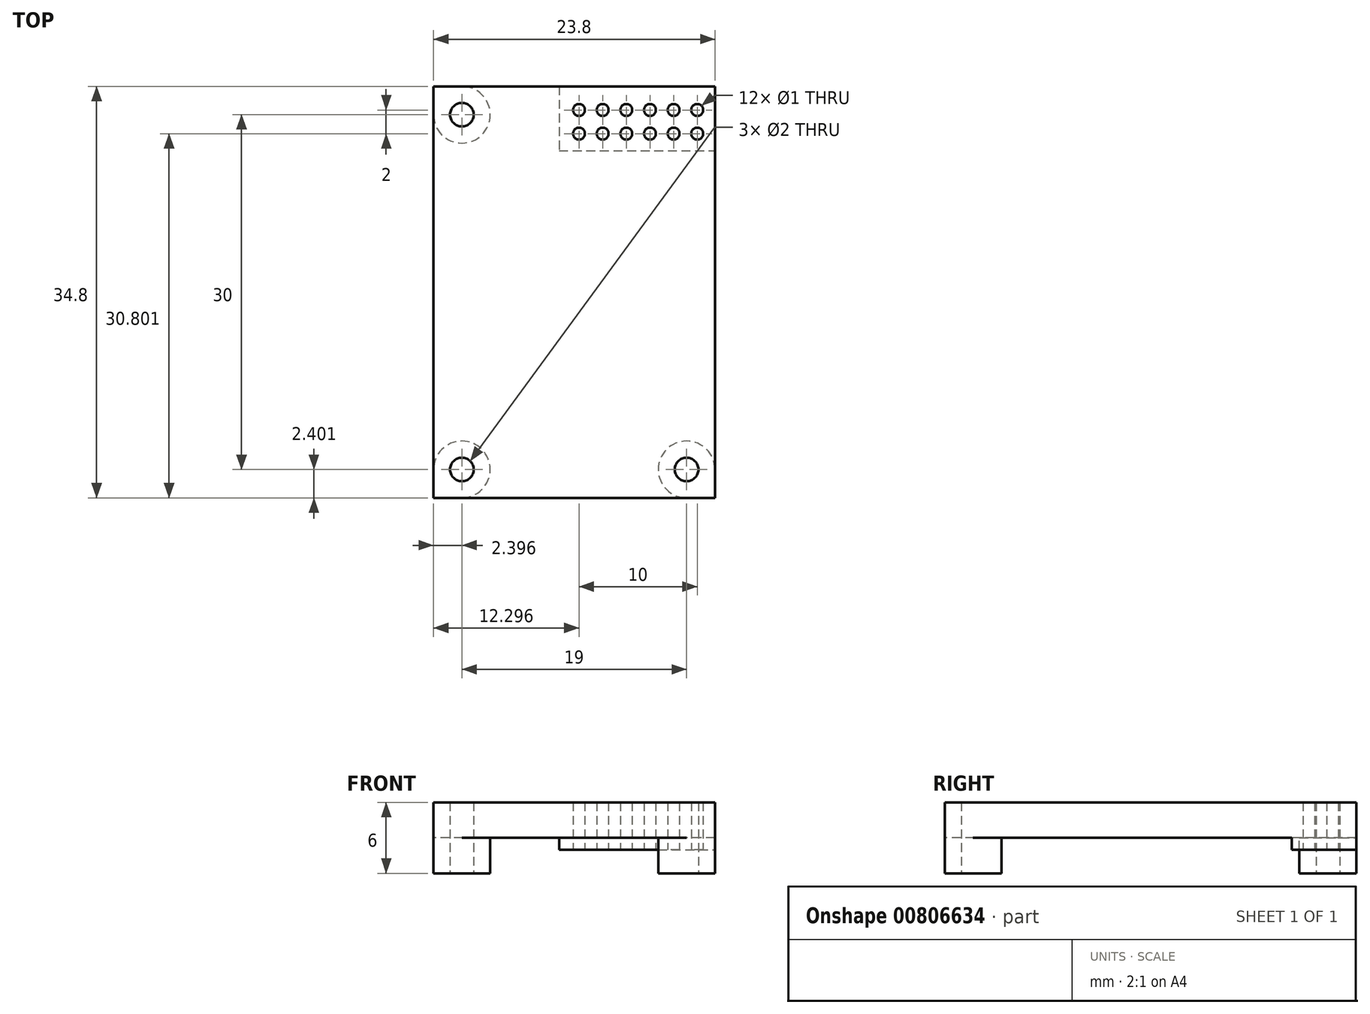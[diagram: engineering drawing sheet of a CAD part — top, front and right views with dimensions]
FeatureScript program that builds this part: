
annotation { "Feature Type Name" : "Feature", "Feature Type Description" : "" }
export const myFeature = defineFeature(function(context is Context, id is Id, definition is map)
    precondition{}
    {
        {
            var Q0;
            Q0=qCreatedBy(makeId("Top.planeOp"),FACE);
            var sketch = newSketch(context, id + "F0", { "sketchPlane" : qUnion([Q0])});
            skLineSegment(sketch, "E0.bottom", {"start": v(-2.78, 3.21) * mm, "end": v(21.02, 3.21) * mm});
            skLineSegment(sketch, "E0.top", {"start": v(-2.78, -31.59) * mm, "end": v(21.02, -31.59) * mm});
            skLineSegment(sketch, "E0.left", {"start": v(-2.78, 3.21) * mm, "end": v(-2.78, -31.59) * mm});
            skLineSegment(sketch, "E0.right", {"start": v(21.02, 3.21) * mm, "end": v(21.02, -31.59) * mm});
            skLineSegment(sketch, "E1", {"start": v(8.52, 3.21) * mm, "end": v(8.52, -1.29) * mm, "construction": true});
            skLineSegment(sketch, "E2", {"start": v(8.52, -1.29) * mm, "end": v(21.02, -1.29) * mm, "construction": true});
            skCircle(sketch, "E3", {"center": v(9.52, -0.79) * mm, "radius": 0.5 * mm});
            skCircle(sketch, "E4.1.0.0", {"center": v(11.52, -0.79) * mm, "radius": 0.5 * mm});
            skCircle(sketch, "E4.2.0.0", {"center": v(13.52, -0.79) * mm, "radius": 0.5 * mm});
            skCircle(sketch, "E4.3.0.0", {"center": v(15.52, -0.79) * mm, "radius": 0.5 * mm});
            skCircle(sketch, "E4.4.0.0", {"center": v(17.52, -0.79) * mm, "radius": 0.5 * mm});
            skCircle(sketch, "E4.5.0.0", {"center": v(19.52, -0.79) * mm, "radius": 0.5 * mm});
            skLineSegment(sketch, "E4.direction1", {"start": v(9.52, -0.79) * mm, "end": v(11.52, -0.79) * mm, "construction": true});
            skLineSegment(sketch, "E5", {"start": v(8.93, 0.21) * mm, "end": v(19.83, 0.21) * mm, "construction": true});
            skCircle(sketch, "E6.MirrorC", {"center": v(9.52, 1.21) * mm, "radius": 0.5 * mm});
            skCircle(sketch, "E7.MirrorC", {"center": v(11.52, 1.21) * mm, "radius": 0.5 * mm});
            skCircle(sketch, "E8.MirrorC", {"center": v(13.52, 1.21) * mm, "radius": 0.5 * mm});
            skCircle(sketch, "E9.MirrorC", {"center": v(15.52, 1.21) * mm, "radius": 0.5 * mm});
            skCircle(sketch, "E10.MirrorC", {"center": v(17.52, 1.21) * mm, "radius": 0.5 * mm});
            skCircle(sketch, "E11.MirrorC", {"center": v(19.52, 1.21) * mm, "radius": 0.5 * mm});
            skLineSegment(sketch, "E12", {"start": v(-2.78, -14.19) * mm, "end": v(21.02, -14.19) * mm, "construction": true});
            skLineSegment(sketch, "E13", {"start": v(9.12, -31.59) * mm, "end": v(9.12, 3.21) * mm, "construction": true});
            skLineSegment(sketch, "E14.bottom", {"start": v(-0.38, 0.81) * mm, "end": v(18.62, 0.81) * mm, "construction": true});
            skLineSegment(sketch, "E14.top", {"start": v(-0.38, -29.19) * mm, "end": v(18.62, -29.19) * mm, "construction": true});
            skLineSegment(sketch, "E14.left", {"start": v(-0.38, 0.81) * mm, "end": v(-0.38, -29.19) * mm, "construction": true});
            skLineSegment(sketch, "E14.right", {"start": v(18.62, 0.81) * mm, "end": v(18.62, -29.19) * mm, "construction": true});
            skPoint(sketch, "E14.middle", {"position": v(9.12, -14.19) * mm});
            skCircle(sketch, "E15", {"center": v(-0.38, 0.81) * mm, "radius": 1 * mm});
            skCircle(sketch, "E16", {"center": v(-0.38, -29.19) * mm, "radius": 1 * mm});
            skCircle(sketch, "E17", {"center": v(18.62, -29.19) * mm, "radius": 1 * mm});
            skSolve(sketch);
        }
        {
            var Q0;
            Q0=qSketchRegion(id+"F0",true);
            extrude(context, id + "F1", {"entities" : qUnion([Q0]), "depth" : 3 * mm, "offsetDistance" : 25 * mm});
        }
        {
            var Q0;
            Q0=makeQuery(id+"F1.opExtrude","CAP_FACE",FACE,{"disambiguationData":[OSD([sQuery(id+"F0.wireOp",EDGE,"E0.bottom"),sQuery(id+"F0.wireOp",EDGE,"E0.top"),sQuery(id+"F0.wireOp",EDGE,"E0.left"),sQuery(id+"F0.wireOp",EDGE,"E0.right"),sQuery(id+"F0.wireOp",EDGE,"E3"),sQuery(id+"F0.wireOp",EDGE,"E4.1.0.0"),sQuery(id+"F0.wireOp",EDGE,"E4.2.0.0"),sQuery(id+"F0.wireOp",EDGE,"E4.3.0.0"),sQuery(id+"F0.wireOp",EDGE,"E4.4.0.0"),sQuery(id+"F0.wireOp",EDGE,"E4.5.0.0"),sQuery(id+"F0.wireOp",EDGE,"E6.MirrorC"),sQuery(id+"F0.wireOp",EDGE,"E7.MirrorC"),sQuery(id+"F0.wireOp",EDGE,"E8.MirrorC"),sQuery(id+"F0.wireOp",EDGE,"E9.MirrorC"),sQuery(id+"F0.wireOp",EDGE,"E10.MirrorC"),sQuery(id+"F0.wireOp",EDGE,"E11.MirrorC"),sQuery(id+"F0.wireOp",EDGE,"E15"),sQuery(id+"F0.wireOp",EDGE,"E16"),sQuery(id+"F0.wireOp",EDGE,"E17")])],"isStart":false});
            var sketch = newSketch(context, id + "F2", { "sketchPlane" : qUnion([Q0])});
            skCircle(sketch, "E18.0", {"center": v(9.52, -0.79) * mm, "radius": 0.5 * mm});
            skCircle(sketch, "E18.1", {"center": v(9.52, 1.21) * mm, "radius": 0.5 * mm});
            skCircle(sketch, "E18.2", {"center": v(11.52, 1.21) * mm, "radius": 0.5 * mm});
            skCircle(sketch, "E18.3", {"center": v(11.52, -0.79) * mm, "radius": 0.5 * mm});
            skCircle(sketch, "E18.4", {"center": v(13.52, -0.79) * mm, "radius": 0.5 * mm});
            skCircle(sketch, "E18.5", {"center": v(13.52, 1.21) * mm, "radius": 0.5 * mm});
            skCircle(sketch, "E18.6", {"center": v(15.52, 1.21) * mm, "radius": 0.5 * mm});
            skCircle(sketch, "E18.7", {"center": v(15.52, -0.79) * mm, "radius": 0.5 * mm});
            skCircle(sketch, "E18.8", {"center": v(17.52, -0.79) * mm, "radius": 0.5 * mm});
            skCircle(sketch, "E18.9", {"center": v(17.52, 1.21) * mm, "radius": 0.5 * mm});
            skCircle(sketch, "E18.10", {"center": v(19.52, 1.21) * mm, "radius": 0.5 * mm});
            skCircle(sketch, "E18.11", {"center": v(19.52, -0.79) * mm, "radius": 0.5 * mm});
            skCircle(sketch, "E18.12", {"center": v(-0.38, 0.81) * mm, "radius": 1 * mm});
            skCircle(sketch, "E18.13", {"center": v(-0.38, -29.19) * mm, "radius": 1 * mm});
            skCircle(sketch, "E18.14", {"center": v(18.62, -29.19) * mm, "radius": 1 * mm});
            skLineSegment(sketch, "E19.0", {"start": v(-2.78, 3.21) * mm, "end": v(21.02, 3.21) * mm});
            skLineSegment(sketch, "E19.1", {"start": v(21.02, 3.21) * mm, "end": v(21.02, -31.59) * mm});
            skLineSegment(sketch, "E20", {"start": v(7.84, 3.21) * mm, "end": v(7.84, -2.24) * mm});
            skLineSegment(sketch, "E21", {"start": v(7.84, -2.24) * mm, "end": v(21.02, -2.24) * mm});
            skCircle(sketch, "E22", {"center": v(-0.38, 0.81) * mm, "radius": 2.4 * mm});
            skCircle(sketch, "E23", {"center": v(-0.38, -29.19) * mm, "radius": 2.4 * mm});
            skCircle(sketch, "E24", {"center": v(18.62, -29.19) * mm, "radius": 2.4 * mm});
            skSolve(sketch);
        }
        {
            var Q0;
            Q0=makeQuery(id+"F2.imprint","IMPRINT",FACE,{"disambiguationData":[TD([[makeQuery(id+"F2.imprint","IMPRINT",EDGE,{"derivedFrom":sQuery(id+"F2.wireOp",EDGE,"E18.0")}),-1.0]])]});
            extrude(context, id + "F3", {"entities" : qUnion([Q0]), "operationType" : NewBodyOperationType.ADD, "oppositeDirection" : true, "depth" : 4 * mm, "offsetDistance" : 25 * mm});
        }
        {
            var Q0;
            Q0=makeQuery(id+"F2.imprint","IMPRINT",FACE,{"disambiguationData":[TD([[makeQuery(id+"F2.imprint","IMPRINT",EDGE,{"derivedFrom":sQuery(id+"F2.wireOp",EDGE,"E18.12")}),-1.0]])]});
            var Q1;
            Q1=makeQuery(id+"F2.imprint","IMPRINT",FACE,{"disambiguationData":[TD([[makeQuery(id+"F2.imprint","IMPRINT",EDGE,{"derivedFrom":sQuery(id+"F2.wireOp",EDGE,"E18.13")}),-1.0]])]});
            var Q2;
            Q2=makeQuery(id+"F2.imprint","IMPRINT",FACE,{"disambiguationData":[TD([[makeQuery(id+"F2.imprint","IMPRINT",EDGE,{"derivedFrom":sQuery(id+"F2.wireOp",EDGE,"E18.14")}),-1.0]])]});
            var Q3;
            {var subQ0=sQuery(id+"F2.wireOp",EDGE,"E19.1");var subQ1=makeQuery(id+"F1.opExtrude","CAP_EDGE",EDGE,{"disambiguationData":[OSD([sQuery(id+"F0.wireOp",EDGE,"E0.top")])],"isStart":false});var subQ2=makeQuery(id+"F2.imprint","INTERSECT",VERTEX,{"derivedFrom":[subQ1,subQ0]});Q3=makeQuery(id+"F2.imprint","IMPRINT",FACE,{"disambiguationData":[TD([[makeQuery(id+"F2.imprint","IMPRINT",EDGE,{"disambiguationData":[TD([[subQ2,1.0]])],"derivedFrom":subQ0}),-1.0]])]});}
            var Q4;
            {var subQ0=sQuery(id+"F2.wireOp",EDGE,"E23");var subQ1=makeQuery(id+"F1.opExtrude","CAP_EDGE",EDGE,{"disambiguationData":[OSD([sQuery(id+"F0.wireOp",EDGE,"E0.top")])],"isStart":false});var subQ2=makeQuery(id+"F2.imprint","INTERSECT",VERTEX,{"derivedFrom":[subQ1,subQ0]});Q4=makeQuery(id+"F2.imprint","IMPRINT",FACE,{"disambiguationData":[TD([[makeQuery(id+"F2.imprint","IMPRINT",EDGE,{"disambiguationData":[TD([[subQ2,1.0]])],"derivedFrom":subQ0}),-1.0]])]});}
            var Q5;
            {var subQ0=sQuery(id+"F2.wireOp",EDGE,"E19.0");var subQ1=makeQuery(id+"F1.opExtrude","CAP_EDGE",EDGE,{"disambiguationData":[OSD([sQuery(id+"F0.wireOp",EDGE,"E0.left")])],"isStart":false});var subQ2=makeQuery(id+"F2.imprint","INTERSECT",VERTEX,{"derivedFrom":[subQ1,subQ0]});Q5=makeQuery(id+"F2.imprint","IMPRINT",FACE,{"disambiguationData":[TD([[makeQuery(id+"F2.imprint","IMPRINT",EDGE,{"disambiguationData":[TD([[subQ2,-1.0]])],"derivedFrom":subQ0}),-1.0]])]});}
            extrude(context, id + "F4", {"entities" : qUnion([Q0, Q1, Q2, Q3, Q4, Q5]), "operationType" : NewBodyOperationType.ADD, "oppositeDirection" : true, "depth" : 6 * mm, "offsetDistance" : 25 * mm});
        }
    });
